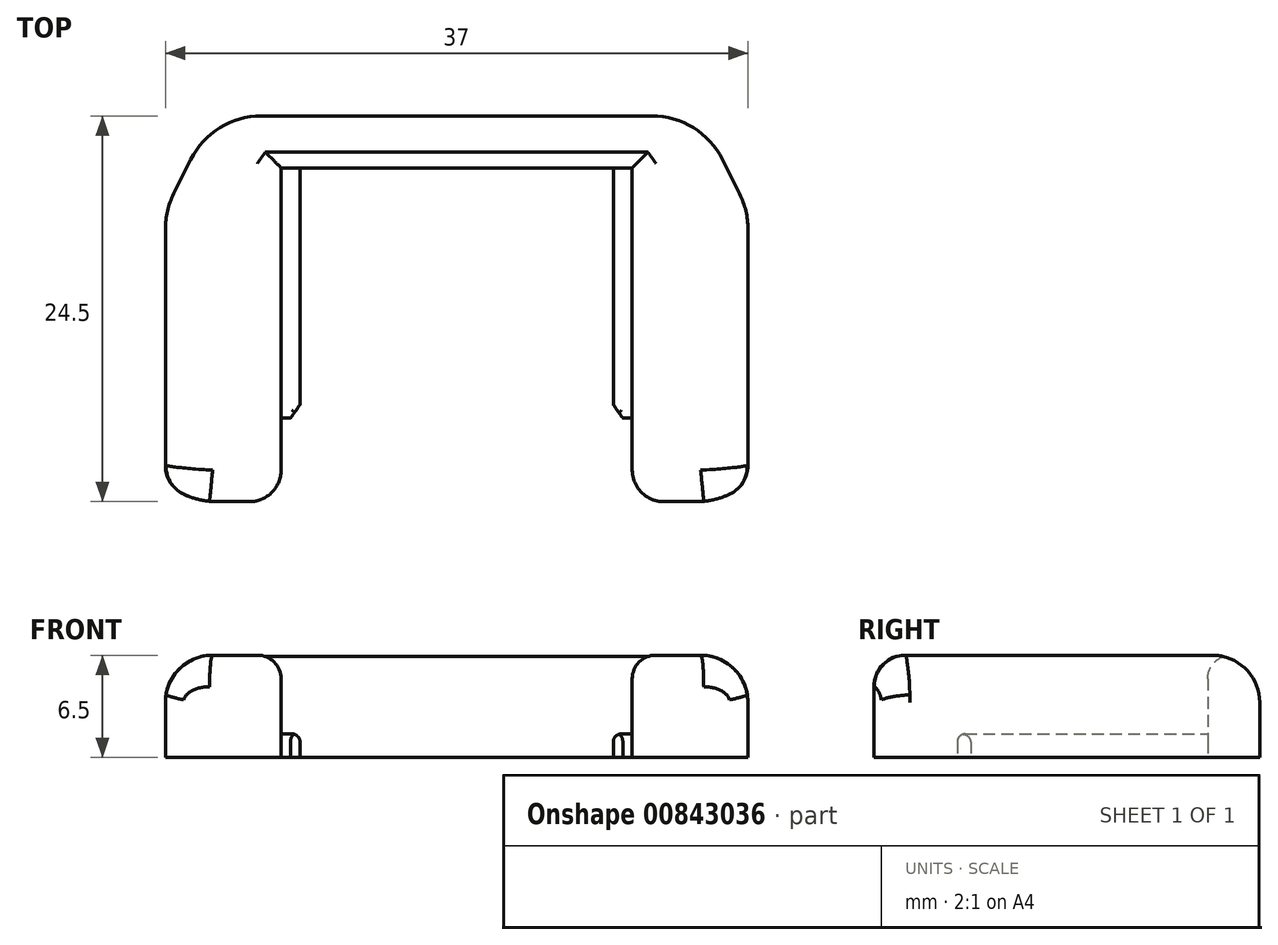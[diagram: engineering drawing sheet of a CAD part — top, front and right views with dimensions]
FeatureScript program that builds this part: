
annotation { "Feature Type Name" : "Feature", "Feature Type Description" : "" }
export const myFeature = defineFeature(function(context is Context, id is Id, definition is map)
    precondition{}
    {
        {
            var Q0;
            Q0=qCreatedBy(makeId("Top.planeOp"),FACE);
            var sketch = newSketch(context, id + "F0", { "sketchPlane" : qUnion([Q0])});
            skLineSegment(sketch, "E0", {"start": v(16.88, 10.04) * mm, "end": v(17.97, 7.86) * mm});
            skLineSegment(sketch, "E1", {"start": v(12.4, 12.8) * mm, "end": v(0, 12.8) * mm});
            skPoint(sketch, "E2.visualSharp", {"position": v(15.5, 12.8) * mm});
            skArc(sketch, "E2.filletArc", {"start": v(16.88, 10.04) * mm, "mid": v(15.04, 12.05) * mm, "end": v(12.4, 12.8) * mm});
            skPoint(sketch, "E3.visualSharp", {"position": v(18.5, 6.8) * mm});
            skArc(sketch, "E3.filletArc", {"start": v(18.5, 5.62) * mm, "mid": v(18.37, 6.77) * mm, "end": v(17.97, 7.86) * mm});
            skLineSegment(sketch, "E4", {"start": v(17.34, -11.22) * mm, "end": v(18.5, -10.68) * mm});
            skLineSegment(sketch, "E5", {"start": v(18.5, 5.62) * mm, "end": v(18.5, -10.68) * mm});
            skPoint(sketch, "E6.visualSharp", {"position": v(16.33, -11.7) * mm});
            skArc(sketch, "E6.filletArc", {"start": v(15.2, -11.7) * mm, "mid": v(16.3, -11.58) * mm, "end": v(17.34, -11.22) * mm});
            skLineSegment(sketch, "E7", {"start": v(11.15, -11.7) * mm, "end": v(11.15, -6.4) * mm});
            skLineSegment(sketch, "E8", {"start": v(9.95, 9.5) * mm, "end": v(0, 9.5) * mm});
            skLineSegment(sketch, "E9", {"start": v(9.95, -5.53) * mm, "end": v(10.55, -6.4) * mm});
            skLineSegment(sketch, "E10", {"start": v(11.15, -6.4) * mm, "end": v(10.55, -6.4) * mm});
            skLineSegment(sketch, "E11", {"start": v(9.95, -5.53) * mm, "end": v(9.95, 9.5) * mm});
            skLineSegment(sketch, "E12", {"start": v(15.2, -11.7) * mm, "end": v(11.15, -11.7) * mm});
            skLineSegment(sketch, "E13.MirrorCS", {"start": v(-12.4, 12.8) * mm, "end": v(0, 12.8) * mm});
            skArc(sketch, "E14.MirrorCS", {"start": v(-16.88, 10.04) * mm, "mid": v(-15.04, 12.05) * mm, "end": v(-12.4, 12.8) * mm});
            skLineSegment(sketch, "E15.MirrorCS", {"start": v(-16.88, 10.04) * mm, "end": v(-17.97, 7.86) * mm});
            skArc(sketch, "E16.MirrorCS", {"start": v(-18.5, 5.62) * mm, "mid": v(-18.37, 6.77) * mm, "end": v(-17.97, 7.86) * mm});
            skLineSegment(sketch, "E17.MirrorCS", {"start": v(-18.5, 5.62) * mm, "end": v(-18.5, -10.68) * mm});
            skLineSegment(sketch, "E18.MirrorCS", {"start": v(-17.34, -11.22) * mm, "end": v(-18.5, -10.68) * mm});
            skArc(sketch, "E19.MirrorCS", {"start": v(-15.2, -11.7) * mm, "mid": v(-16.3, -11.58) * mm, "end": v(-17.34, -11.22) * mm});
            skLineSegment(sketch, "E20.MirrorCS", {"start": v(-15.2, -11.7) * mm, "end": v(-11.15, -11.7) * mm});
            skLineSegment(sketch, "E21.MirrorCS", {"start": v(-11.15, -11.7) * mm, "end": v(-11.15, -6.4) * mm});
            skLineSegment(sketch, "E22.MirrorCS", {"start": v(-11.15, -6.4) * mm, "end": v(-10.55, -6.4) * mm});
            skLineSegment(sketch, "E23.MirrorCS", {"start": v(-9.95, -5.53) * mm, "end": v(-10.55, -6.4) * mm});
            skLineSegment(sketch, "E24.MirrorCS", {"start": v(-9.95, -5.53) * mm, "end": v(-9.95, 9.5) * mm});
            skLineSegment(sketch, "E25.MirrorCS", {"start": v(-9.95, 9.5) * mm, "end": v(0, 9.5) * mm});
            skSolve(sketch);
        }
        {
            var Q0;
            Q0=makeQuery(id+"F0.imprint","IMPRINT",FACE,{"disambiguationData":[TD([[makeQuery(id+"F0.imprint","IMPRINT",EDGE,{"derivedFrom":sQuery(id+"F0.wireOp",EDGE,"E0")}),-1.0]])]});
            extrude(context, id + "F1", {"entities" : qUnion([Q0]), "depth" : 1.5 * mm, "offsetDistance" : 25 * mm});
        }
        {
            var Q0;
            Q0=makeQuery(id+"F1.opExtrude","CAP_FACE",FACE,{"disambiguationData":[OSD([sQuery(id+"F0.wireOp",EDGE,"E0"),sQuery(id+"F0.wireOp",EDGE,"E1"),sQuery(id+"F0.wireOp",EDGE,"E2.filletArc"),sQuery(id+"F0.wireOp",EDGE,"E3.filletArc"),sQuery(id+"F0.wireOp",EDGE,"E4"),sQuery(id+"F0.wireOp",EDGE,"E5"),sQuery(id+"F0.wireOp",EDGE,"E6.filletArc"),sQuery(id+"F0.wireOp",EDGE,"E7"),sQuery(id+"F0.wireOp",EDGE,"E8"),sQuery(id+"F0.wireOp",EDGE,"E9"),sQuery(id+"F0.wireOp",EDGE,"E10"),sQuery(id+"F0.wireOp",EDGE,"E11"),sQuery(id+"F0.wireOp",EDGE,"E12"),sQuery(id+"F0.wireOp",EDGE,"E13.MirrorCS"),sQuery(id+"F0.wireOp",EDGE,"E14.MirrorCS"),sQuery(id+"F0.wireOp",EDGE,"E15.MirrorCS"),sQuery(id+"F0.wireOp",EDGE,"E16.MirrorCS"),sQuery(id+"F0.wireOp",EDGE,"E17.MirrorCS"),sQuery(id+"F0.wireOp",EDGE,"E18.MirrorCS"),sQuery(id+"F0.wireOp",EDGE,"E19.MirrorCS"),sQuery(id+"F0.wireOp",EDGE,"E20.MirrorCS"),sQuery(id+"F0.wireOp",EDGE,"E21.MirrorCS"),sQuery(id+"F0.wireOp",EDGE,"E22.MirrorCS"),sQuery(id+"F0.wireOp",EDGE,"E23.MirrorCS"),sQuery(id+"F0.wireOp",EDGE,"E24.MirrorCS"),sQuery(id+"F0.wireOp",EDGE,"E25.MirrorCS")])],"isStart":false});
            var sketch = newSketch(context, id + "F2", { "sketchPlane" : qUnion([Q0])});
            skLineSegment(sketch, "E26", {"start": v(16.88, 10.04) * mm, "end": v(17.97, 7.86) * mm});
            skLineSegment(sketch, "E27", {"start": v(12.4, 12.8) * mm, "end": v(0, 12.8) * mm});
            skPoint(sketch, "E28.visualSharp", {"position": v(15.5, 12.8) * mm});
            skArc(sketch, "E28.filletArc", {"start": v(16.88, 10.04) * mm, "mid": v(15.04, 12.05) * mm, "end": v(12.4, 12.8) * mm});
            skPoint(sketch, "E29.visualSharp", {"position": v(18.5, 6.8) * mm});
            skArc(sketch, "E29.filletArc", {"start": v(18.5, 5.62) * mm, "mid": v(18.37, 6.77) * mm, "end": v(17.97, 7.86) * mm});
            skLineSegment(sketch, "E30", {"start": v(17.34, -11.22) * mm, "end": v(18.5, -10.68) * mm});
            skLineSegment(sketch, "E31", {"start": v(18.5, 5.62) * mm, "end": v(18.5, -10.68) * mm});
            skPoint(sketch, "E32.visualSharp", {"position": v(16.33, -11.7) * mm});
            skArc(sketch, "E32.filletArc", {"start": v(15.2, -11.7) * mm, "mid": v(16.3, -11.58) * mm, "end": v(17.34, -11.22) * mm});
            skLineSegment(sketch, "E33", {"start": v(15.2, -11.7) * mm, "end": v(11.15, -11.7) * mm});
            skLineSegment(sketch, "E34", {"start": v(11.15, -11.7) * mm, "end": v(11.15, 9.5) * mm});
            skLineSegment(sketch, "E35", {"start": v(11.15, 9.5) * mm, "end": v(0, 9.5) * mm});
            skLineSegment(sketch, "E36.MirrorCS", {"start": v(-12.4, 12.8) * mm, "end": v(0, 12.8) * mm});
            skArc(sketch, "E37.MirrorCS", {"start": v(-16.88, 10.04) * mm, "mid": v(-15.04, 12.05) * mm, "end": v(-12.4, 12.8) * mm});
            skLineSegment(sketch, "E38.MirrorCS", {"start": v(-16.88, 10.04) * mm, "end": v(-17.97, 7.86) * mm});
            skArc(sketch, "E39.MirrorCS", {"start": v(-18.5, 5.62) * mm, "mid": v(-18.37, 6.77) * mm, "end": v(-17.97, 7.86) * mm});
            skLineSegment(sketch, "E40.MirrorCS", {"start": v(-18.5, 5.62) * mm, "end": v(-18.5, -10.68) * mm});
            skLineSegment(sketch, "E41.MirrorCS", {"start": v(-17.34, -11.22) * mm, "end": v(-18.5, -10.68) * mm});
            skArc(sketch, "E42.MirrorCS", {"start": v(-15.2, -11.7) * mm, "mid": v(-16.3, -11.58) * mm, "end": v(-17.34, -11.22) * mm});
            skLineSegment(sketch, "E43.MirrorCS", {"start": v(-15.2, -11.7) * mm, "end": v(-11.15, -11.7) * mm});
            skLineSegment(sketch, "E44.MirrorCS", {"start": v(-11.15, -11.7) * mm, "end": v(-11.15, 9.5) * mm});
            skLineSegment(sketch, "E45.MirrorCS", {"start": v(-11.15, 9.5) * mm, "end": v(0, 9.5) * mm});
            skSolve(sketch);
        }
        {
            var Q0;
            Q0 = qSketchRegion(id + "F2", true);
            extrude(context, id + "F3", {"entities" : qUnion([Q0]), "operationType" : NewBodyOperationType.ADD, "depth" : 5 * mm, "offsetDistance" : 25 * mm});
        }
        {
            var Q0;
            Q0=makeQuery(id+"F3.opExtrude","CAP_EDGE",EDGE,{"disambiguationData":[OSD([sQuery(id+"F2.wireOp",EDGE,"E34")])],"isStart":false});
            var Q1;
            Q1=makeQuery(id+"F3.opExtrude","CAP_EDGE",EDGE,{"disambiguationData":[OSD([sQuery(id+"F2.wireOp",EDGE,"E35"),sQuery(id+"F2.wireOp",EDGE,"E45.MirrorCS")])],"isStart":false});
            var Q2;
            Q2=makeQuery(id+"F3.opExtrude","CAP_EDGE",EDGE,{"disambiguationData":[OSD([sQuery(id+"F2.wireOp",EDGE,"E44.MirrorCS")])],"isStart":false});
            fillet(context, id + "F4", {"entities" : qUnion([Q0, Q1, Q2]), "radius" : 1.5 * mm, "tangentPropagation" : true, "allowEdgeOverflow" : false});
        }
        {
            var Q0;
            Q0=makeQuery(id+"F3.opExtrude","CAP_EDGE",EDGE,{"disambiguationData":[OSD([sQuery(id+"F2.wireOp",EDGE,"E40.MirrorCS")])],"isStart":false});
            fillet(context, id + "F5", {"entities" : qUnion([Q0]), "radius" : 3 * mm, "tangentPropagation" : true, "allowEdgeOverflow" : false});
        }
        {
            var Q0;
            Q0=makeQuery(id+"F3.opExtrude","CAP_EDGE",EDGE,{"disambiguationData":[OSD([sQuery(id+"F2.wireOp",EDGE,"95c838eb-fbcd-410c-90c5-c648d99ee7404.MirrorCS")])],"isStart":false});
            var Q1;
            Q1=makeQuery(id+"F3.opExtrude","CAP_EDGE",EDGE,{"disambiguationData":[OSD([sQuery(id+"F2.wireOp",EDGE,"9bcd449e-15ee-4000-95ae-8525963fbd04.filletArc")])],"isStart":false});
            var Q2;
            Q2=makeQuery(id+"F5.opFillet","BLEND_EDGE",EDGE,{"blendedFrom":[makeQuery(id+"F3.opExtrude","CAP_EDGE",EDGE,{"disambiguationData":[OSD([sQuery(id+"F2.wireOp",EDGE,"E40.MirrorCS")])],"isStart":false}),makeQuery(id+"F3.boolean.opBoolean","MERGE",FACE,{"derivedFrom":[makeQuery(id+"F1.opExtrude","SWEPT_FACE",FACE,{"disambiguationData":[OSD([sQuery(id+"F0.wireOp",EDGE,"E19.MirrorCS")])]}),makeQuery(id+"F3.opExtrude","SWEPT_FACE",FACE,{"disambiguationData":[OSD([sQuery(id+"F2.wireOp",EDGE,"E42.MirrorCS")])]})]})],"blendedInto":[makeQuery(id+"F3.boolean.opBoolean","MERGE",FACE,{"derivedFrom":[makeQuery(id+"F1.opExtrude","SWEPT_FACE",FACE,{"disambiguationData":[OSD([sQuery(id+"F0.wireOp",EDGE,"E19.MirrorCS")])]}),makeQuery(id+"F3.opExtrude","SWEPT_FACE",FACE,{"disambiguationData":[OSD([sQuery(id+"F2.wireOp",EDGE,"E42.MirrorCS")])]})]})]});
            var Q3;
            Q3=makeQuery(id+"F3.opExtrude","CAP_EDGE",EDGE,{"disambiguationData":[OSD([sQuery(id+"F2.wireOp",EDGE,"E33")])],"isStart":false});
            fillet(context, id + "F6", {"entities" : qUnion([Q0, Q1, Q2, Q3]), "radius" : 2 * mm, "tangentPropagation" : true, "allowEdgeOverflow" : false});
        }
        {
            var Q0;
            Q0=makeQuery(id+"F1.opExtrude","CAP_EDGE",EDGE,{"disambiguationData":[OSD([sQuery(id+"F0.wireOp",EDGE,"E24.MirrorCS")])],"isStart":false});
            var Q1;
            Q1=makeQuery(id+"F1.opExtrude","CAP_EDGE",EDGE,{"disambiguationData":[OSD([sQuery(id+"F0.wireOp",EDGE,"E11")])],"isStart":false});
            var Q2;
            Q2=makeQuery(id+"F1.opExtrude","CAP_EDGE",EDGE,{"disambiguationData":[OSD([sQuery(id+"F0.wireOp",EDGE,"E22.MirrorCS")])],"isStart":false});
            var Q3;
            Q3=makeQuery(id+"F1.opExtrude","CAP_EDGE",EDGE,{"disambiguationData":[OSD([sQuery(id+"F0.wireOp",EDGE,"E10")])],"isStart":false});
            fillet(context, id + "F7", {"entities" : qUnion([Q0, Q1, Q2, Q3]), "radius" : 0.5 * mm, "tangentPropagation" : true, "allowEdgeOverflow" : false});
        }
    });
